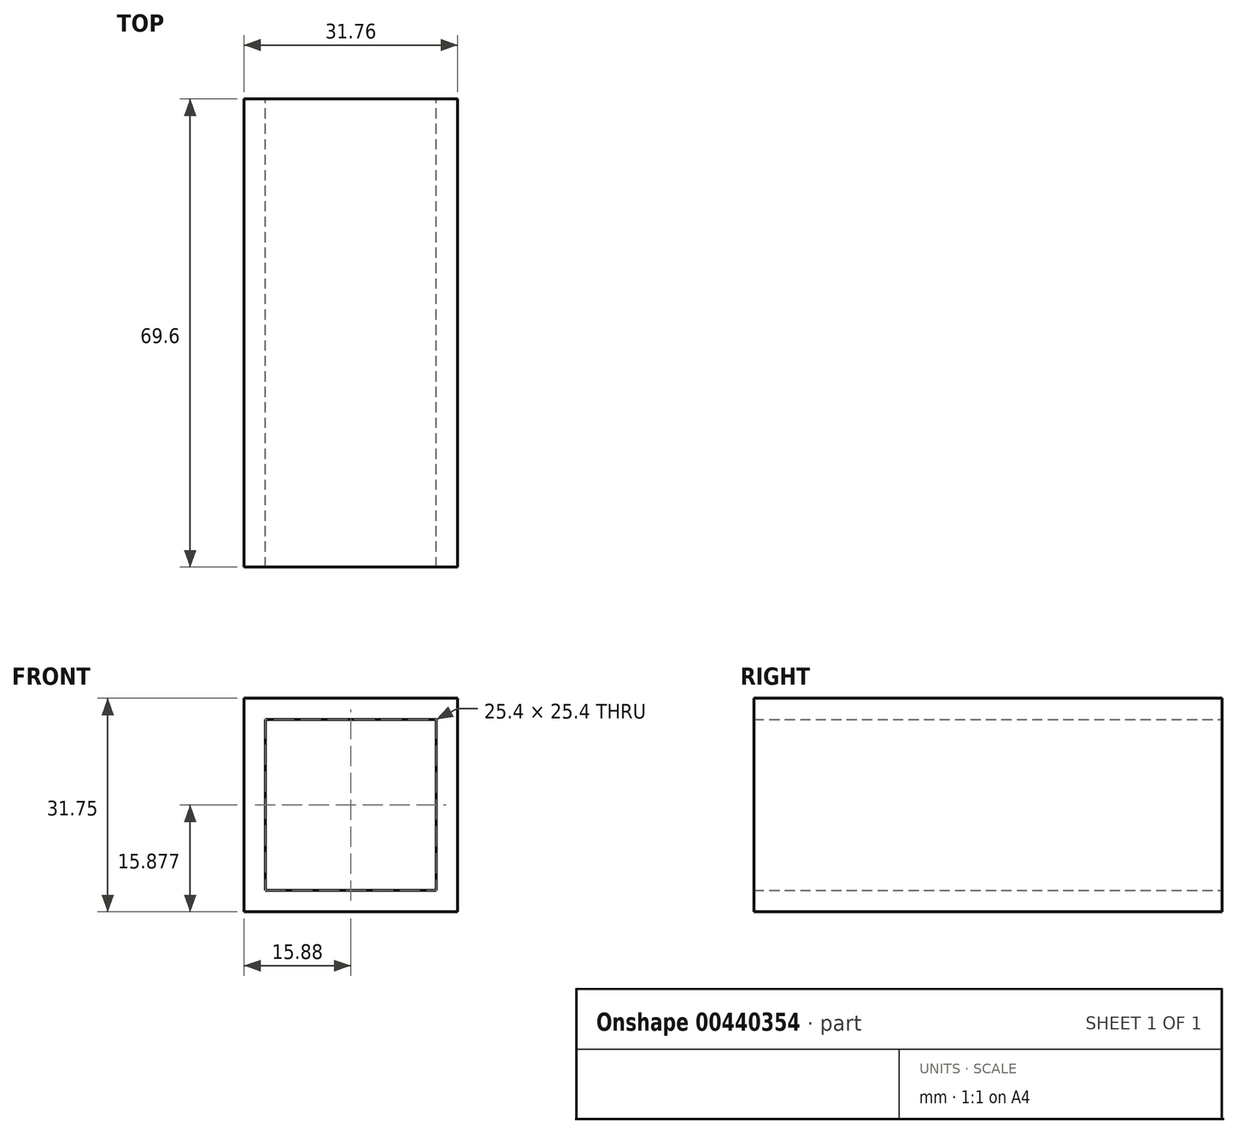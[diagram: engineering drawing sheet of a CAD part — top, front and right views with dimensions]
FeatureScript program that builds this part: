
annotation { "Feature Type Name" : "Feature", "Feature Type Description" : "" }
export const myFeature = defineFeature(function(context is Context, id is Id, definition is map)
    precondition{}
    {
        {
            var Q0;
            Q0=qCreatedBy(makeId("Front.planeOp"),FACE);
            var sketch = newSketch(context, id + "F0", { "sketchPlane" : qUnion([Q0])});
            skLineSegment(sketch, "E0.bottom", {"start": v(-15.88, 12.5) * mm, "end": v(15.88, 12.5) * mm});
            skLineSegment(sketch, "E0.top", {"start": v(-15.88, -19.25) * mm, "end": v(15.88, -19.25) * mm});
            skLineSegment(sketch, "E0.left", {"start": v(-15.88, 12.5) * mm, "end": v(-15.88, -19.25) * mm});
            skLineSegment(sketch, "E0.right", {"start": v(15.88, 12.5) * mm, "end": v(15.87, -19.25) * mm});
            skPoint(sketch, "E0.middle", {"position": v(0, -3.37) * mm});
            skLineSegment(sketch, "E1.bottom", {"start": v(-12.7, 9.33) * mm, "end": v(12.7, 9.33) * mm});
            skLineSegment(sketch, "E1.top", {"start": v(-12.7, -16.07) * mm, "end": v(12.7, -16.07) * mm});
            skLineSegment(sketch, "E1.left", {"start": v(-12.7, 9.33) * mm, "end": v(-12.7, -16.07) * mm});
            skLineSegment(sketch, "E1.right", {"start": v(12.7, 9.33) * mm, "end": v(12.7, -16.07) * mm});
            skSolve(sketch);
        }
        {
            var Q0;
            Q0=makeQuery(id+"F0.imprint","IMPRINT",FACE,{"disambiguationData":[TD([[makeQuery(id+"F0.imprint","IMPRINT",EDGE,{"derivedFrom":sQuery(id+"F0.wireOp",EDGE,"E0.bottom")}),-1.0]])]});
            extrude(context, id + "F1", {"entities" : qUnion([Q0]), "endBound" : BoundingType.SYMMETRIC, "depth" : 69.6 * mm});
        }
    });
